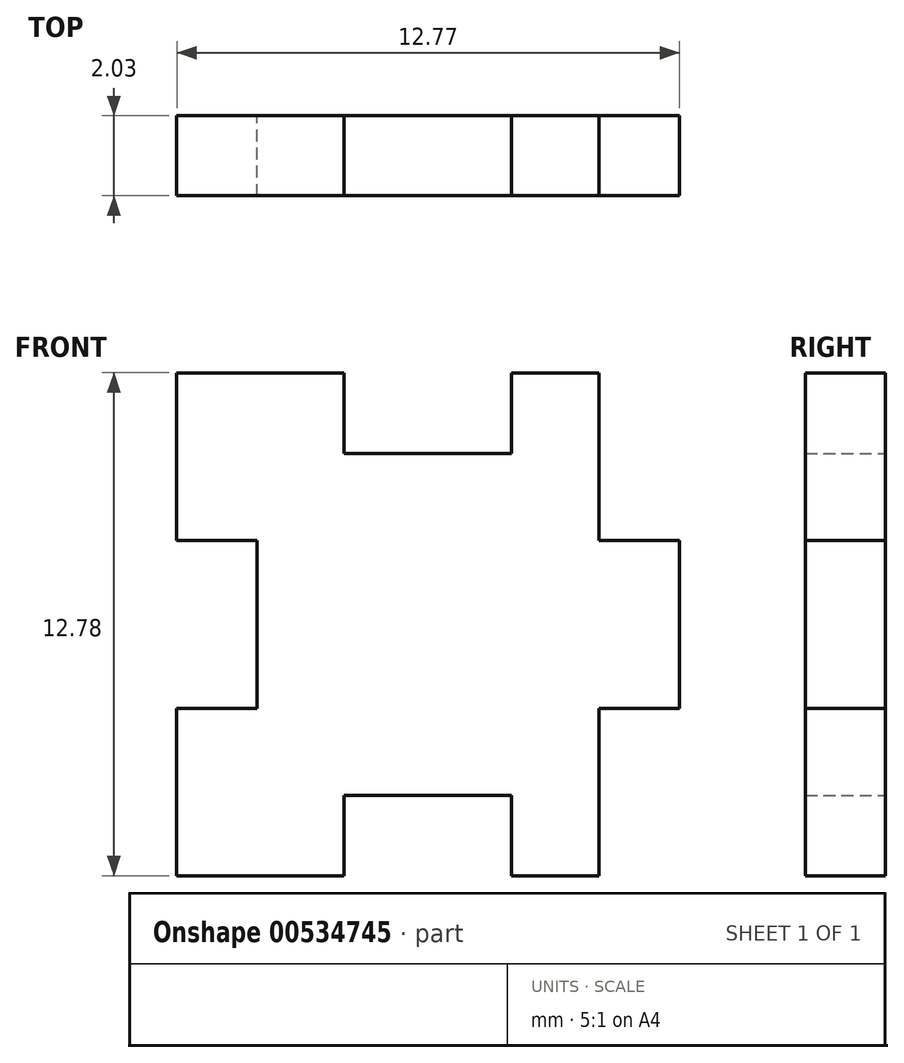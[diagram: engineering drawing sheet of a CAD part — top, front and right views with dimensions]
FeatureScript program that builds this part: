
annotation { "Feature Type Name" : "Feature", "Feature Type Description" : "" }
export const myFeature = defineFeature(function(context is Context, id is Id, definition is map)
    precondition{}
    {
        {
            var Q0;
            Q0=qCreatedBy(makeId("Front.planeOp"),FACE);
            var sketch = newSketch(context, id + "F0", { "sketchPlane" : qUnion([Q0])});
            skLineSegment(sketch, "E0", {"start": v(-10.99, 26.89) * mm, "end": v(-10.99, 29.02) * mm});
            skLineSegment(sketch, "E1", {"start": v(-10.99, 29.02) * mm, "end": v(-13.03, 29.02) * mm});
            skLineSegment(sketch, "E2", {"start": v(-13.03, 29.02) * mm, "end": v(-13.03, 33.28) * mm});
            skLineSegment(sketch, "E3", {"start": v(-13.03, 33.28) * mm, "end": v(-8.78, 33.28) * mm});
            skLineSegment(sketch, "E4", {"start": v(-8.78, 33.28) * mm, "end": v(-8.78, 31.23) * mm});
            skLineSegment(sketch, "E5", {"start": v(-8.78, 31.23) * mm, "end": v(-4.53, 31.23) * mm});
            skLineSegment(sketch, "E6", {"start": v(-4.53, 31.23) * mm, "end": v(-4.53, 33.28) * mm});
            skLineSegment(sketch, "E7", {"start": v(-4.53, 33.28) * mm, "end": v(-2.3, 33.28) * mm});
            skLineSegment(sketch, "E8", {"start": v(-2.3, 33.28) * mm, "end": v(-2.3, 29.02) * mm});
            skLineSegment(sketch, "E9", {"start": v(-2.3, 29.02) * mm, "end": v(-0.26, 29.02) * mm});
            skLineSegment(sketch, "E10", {"start": v(-10.99, 26.89) * mm, "end": v(8.72, 26.89) * mm, "construction": true});
            skLineSegment(sketch, "E11.MirrorCS", {"start": v(-2.3, 24.76) * mm, "end": v(-0.26, 24.76) * mm});
            skLineSegment(sketch, "E12.MirrorCS", {"start": v(-2.3, 20.5) * mm, "end": v(-2.3, 24.76) * mm});
            skLineSegment(sketch, "E13.MirrorCS", {"start": v(-4.53, 20.5) * mm, "end": v(-2.3, 20.5) * mm});
            skLineSegment(sketch, "E14.MirrorCS", {"start": v(-4.53, 22.55) * mm, "end": v(-4.53, 20.5) * mm});
            skLineSegment(sketch, "E15.MirrorCS", {"start": v(-8.78, 22.55) * mm, "end": v(-4.53, 22.55) * mm});
            skLineSegment(sketch, "E16.MirrorCS", {"start": v(-8.78, 20.5) * mm, "end": v(-8.78, 22.55) * mm});
            skLineSegment(sketch, "E17.MirrorCS", {"start": v(-13.03, 20.5) * mm, "end": v(-8.78, 20.5) * mm});
            skLineSegment(sketch, "E18.MirrorCS", {"start": v(-13.03, 24.76) * mm, "end": v(-13.03, 20.5) * mm});
            skLineSegment(sketch, "E19.MirrorCS", {"start": v(-10.99, 24.76) * mm, "end": v(-13.03, 24.76) * mm});
            skLineSegment(sketch, "E20.MirrorCS", {"start": v(-10.99, 26.89) * mm, "end": v(-10.99, 24.76) * mm});
            skLineSegment(sketch, "E21", {"start": v(-0.26, 29.02) * mm, "end": v(-0.26, 24.76) * mm});
            skSolve(sketch);
        }
        {
            var Q0;
            Q0=makeQuery(id+"F0.imprint","IMPRINT",FACE,{"disambiguationData":[TD([[makeQuery(id+"F0.imprint","IMPRINT",EDGE,{"derivedFrom":sQuery(id+"F0.wireOp",EDGE,"E0")}),-1.0]])]});
            extrude(context, id + "F1", {"entities" : qUnion([Q0]), "depth" : 2.03 * mm, "offsetDistance" : 25.4 * mm});
        }
        {
            var Q0;
            Q0=qCreatedBy(makeId("Front.planeOp"),FACE);
            cPlane(context, id + "F2", {"entities" : qUnion([Q0]), "cplaneType" : CPlaneType.OFFSET, "offset" : 4.06 * mm, "width" : 152.4 * mm, "height" : 152.4 * mm});
        }
        {
            var Q0;
            Q0=qCreatedBy(id+"F2.planeOp",FACE);
            var sketch = newSketch(context, id + "F3", { "sketchPlane" : qUnion([Q0])});
            skText(sketch, "E22", { "text": "O", "fontName": "OpenSans-Regular.ttf"});
            const initialGuessF3  = {"E22": [-0.01028, 0.02352, 1, 0, 0.00664]};
            skSetInitialGuess(sketch, initialGuessF3);
            skSolve(sketch);
        }
        {
            var Q0;
            Q0 = qSketchRegion(id + "F3", true);
            extrude(context, id + "F4", {"entities" : qUnion([Q0]), "operationType" : NewBodyOperationType.REMOVE, "oppositeDirection" : true, "depth" : 0.5 * mm, "offsetDistance" : 25.4 * mm});
        }
    });
